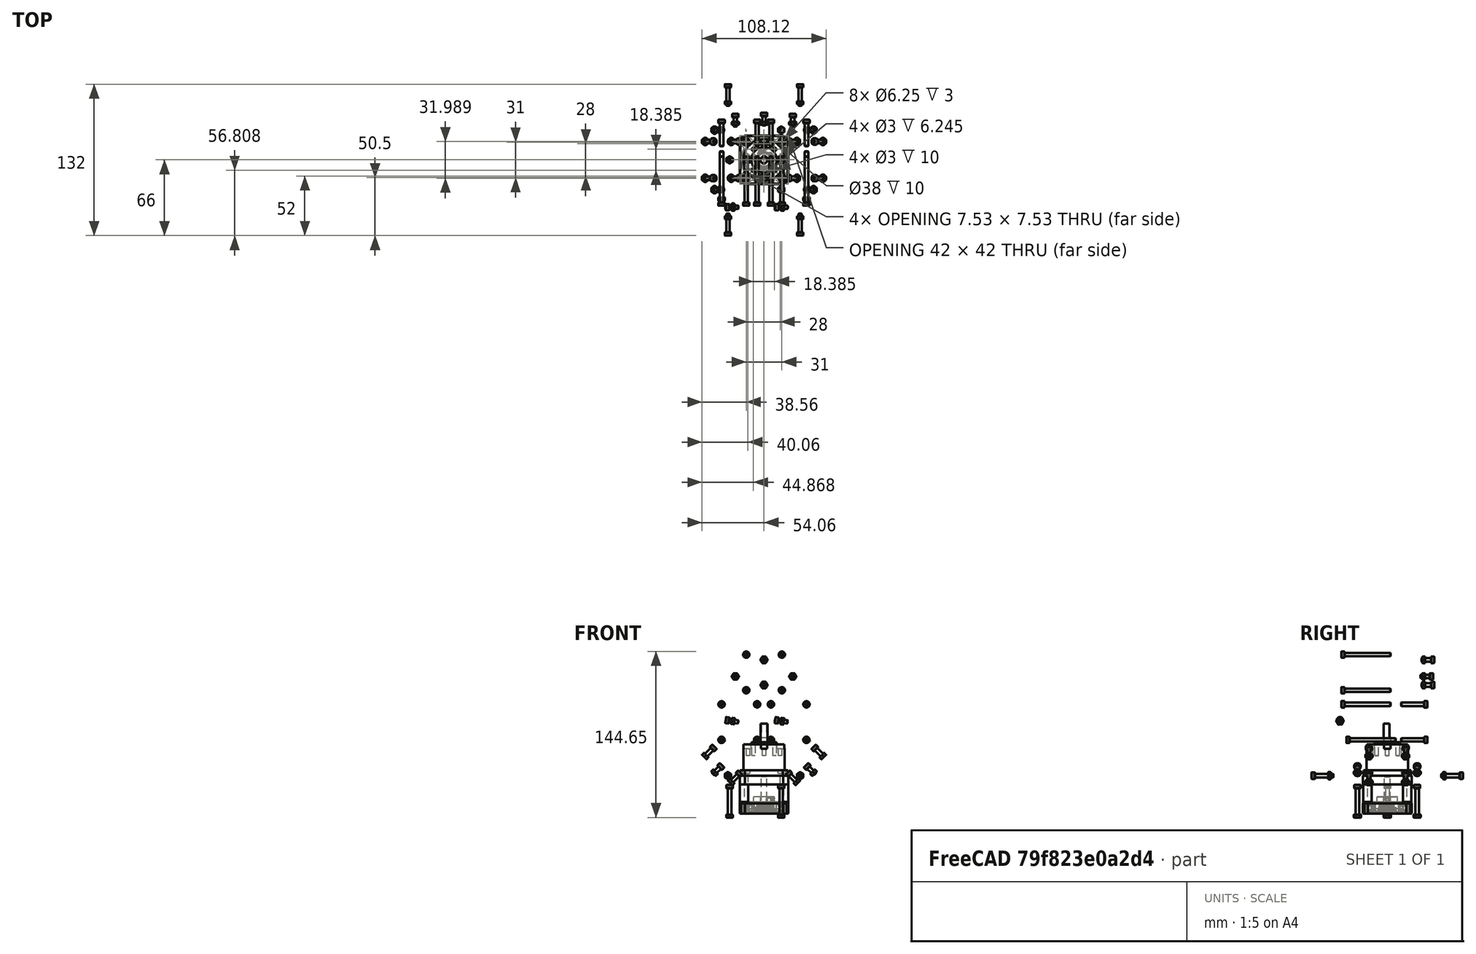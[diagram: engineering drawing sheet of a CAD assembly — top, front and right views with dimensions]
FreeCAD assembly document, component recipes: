
FREECAD ASSEMBLY — COMPONENT RECIPES ("AssemblyArt1")

This assembly document has 6 components, labeled P0..P5 below (a component is one placed body or linked part). 0 of them carry a construction recipe — the FreeCAD feature program that regenerates the part from scratch, quoted from this document or its linked companion documents; the rest are supplied as boundary geometry only. No exploded tour is included for this assembly.
COMPONENT P0 — geometry summary ("Bearing_625ZZ"; no construction recipe available for this part):
  bounding box: 16.0 x 16.0 x 5.0 mm
  tessellated surface: 4,788 triangles
  volume: 876 mm^3 (68% of its bounding box)
  symmetry: 2-fold rotationally symmetric about the x axis; 2-fold rotationally symmetric about the y axis; revolution-symmetric about the z axis through its bounding-box center; mirror-symmetric across its x mid-plane, y mid-plane, z mid-plane
COMPONENT P1 — geometry summary ("Fan_40x40"; no construction recipe available for this part):
  bounding box: 40.0 x 40.0 x 10.0 mm
  tessellated surface: 7,530 triangles
  volume: 6703 mm^3 (42% of its bounding box)
COMPONENT P2 — geometry summary ("Nema17_GearBox"; no construction recipe available for this part):
  bounding box: 78.3 x 42.3 x 42.3 mm
  tessellated surface: 11,192 triangles
  volume: 85844 mm^3 (61% of its bounding box)
  symmetry: mirror-symmetric across its y mid-plane
COMPONENT P3 — geometry summary ("5x14.5mm"; no construction recipe available for this part):
  bounding box: 14.5 x 5.0 x 5.0 mm
  tessellated surface: 500 triangles
  volume: 285 mm^3 (79% of its bounding box)
  symmetry: 2-fold rotationally symmetric about the x axis; 2-fold rotationally symmetric about the y axis; revolution-symmetric about the z axis through its bounding-box center; mirror-symmetric across its y mid-plane, z mid-plane
COMPONENT P4 — geometry summary ("Pulley_GT2x20_Modified"; no construction recipe available for this part):
  bounding box: 18.0 x 18.0 x 14.6 mm
  tessellated surface: 5,648 triangles
  volume: 2210 mm^3 (47% of its bounding box)
  symmetry: mirror-symmetric across its y mid-plane
COMPONENT P5 — geometry summary ("5x32mm"; no construction recipe available for this part):
  bounding box: 32.0 x 5.0 x 5.0 mm
  tessellated surface: 500 triangles
  volume: 628 mm^3 (79% of its bounding box)
  symmetry: 2-fold rotationally symmetric about the x axis; 2-fold rotationally symmetric about the y axis; 3-fold rotationally symmetric about the z axis; mirror-symmetric across its x mid-plane, y mid-plane, z mid-plane
PROVENANCE & LICENSES
A FreeCAD (.FCStd) document from a public repository crawl; recipes are the document's own serialized feature recipes (and, for linked parts, companion documents' recipes).
License: as declared in the source repository (recorded in the dataset sidecar).
